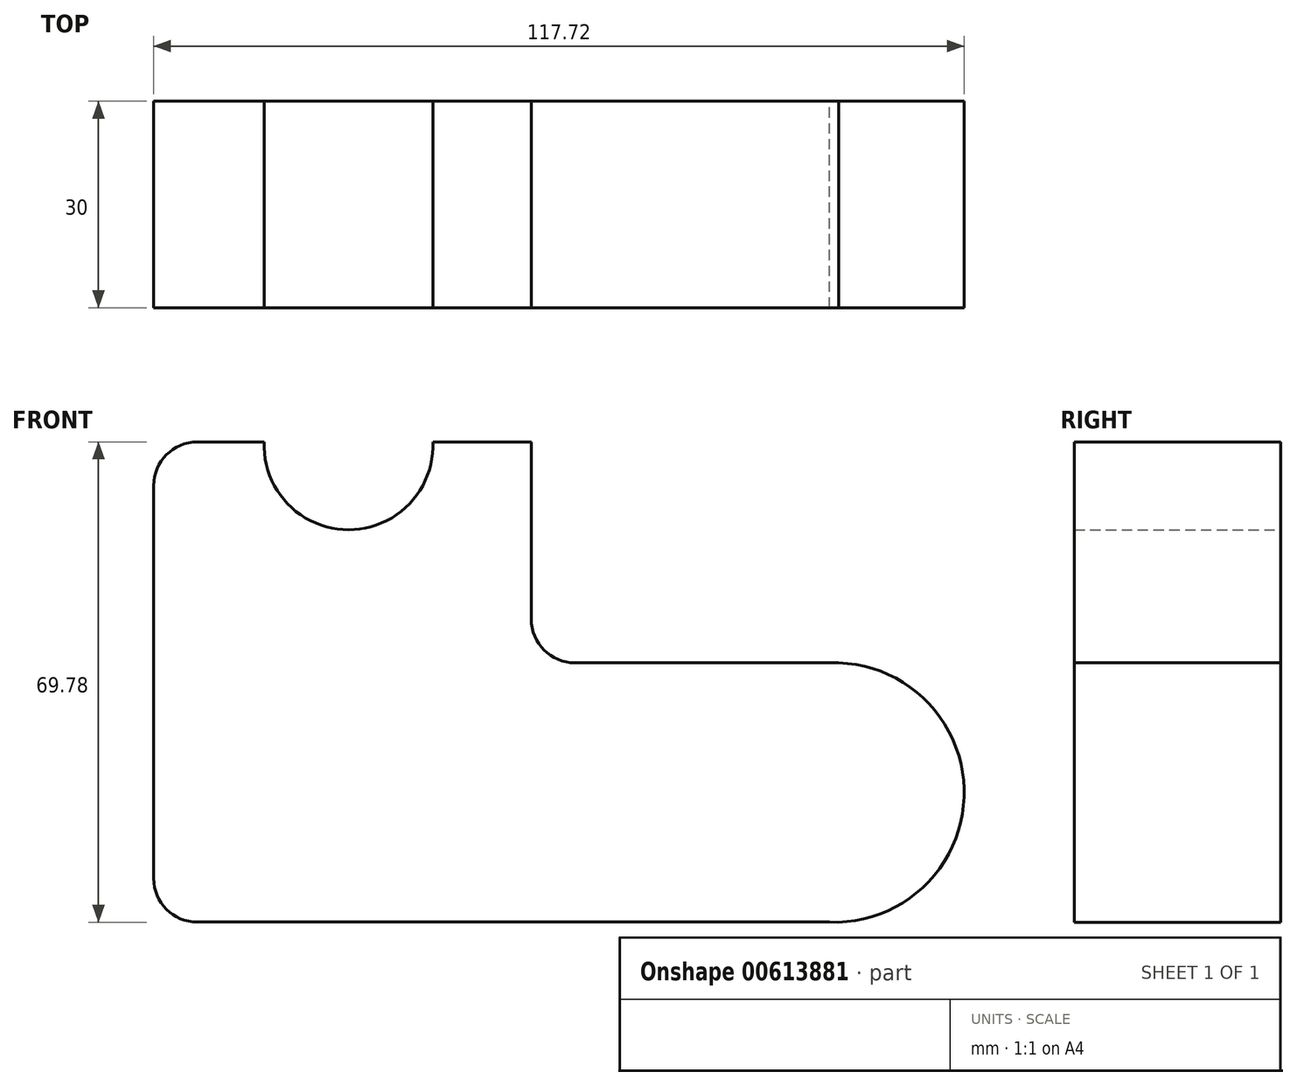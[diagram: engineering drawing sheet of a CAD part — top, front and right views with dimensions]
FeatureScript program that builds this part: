
annotation { "Feature Type Name" : "Feature", "Feature Type Description" : "" }
export const myFeature = defineFeature(function(context is Context, id is Id, definition is map)
    precondition{}
    {
        {
            var Q0;
            Q0=qCreatedBy(makeId("Front.planeOp"),FACE);
            var sketch = newSketch(context, id + "F0", { "sketchPlane" : qUnion([Q0])});
            skLineSegment(sketch, "E0", {"start": v(-14.34, 0) * mm, "end": v(-107.56, 0) * mm});
            skLineSegment(sketch, "E1", {"start": v(-113.9, 6.35) * mm, "end": v(-113.9, 63.42) * mm});
            skLineSegment(sketch, "E2", {"start": v(-107.56, 69.77) * mm, "end": v(-97.86, 69.77) * mm});
            skLineSegment(sketch, "E3", {"start": v(-59.07, 69.77) * mm, "end": v(-59.07, 44.02) * mm});
            skLineSegment(sketch, "E4", {"start": v(-52.72, 37.67) * mm, "end": v(-14.4, 37.67) * mm});
            skLineSegment(sketch, "E5", {"start": v(0, 31.32) * mm, "end": v(0, 30.2) * mm});
            skPoint(sketch, "E6.visualSharp", {"position": v(-113.9, 69.77) * mm});
            skArc(sketch, "E6.filletArc", {"start": v(-107.56, 69.77) * mm, "mid": v(-112.05, 67.91) * mm, "end": v(-113.9, 63.42) * mm});
            skPoint(sketch, "E7.visualSharp", {"position": v(-113.9, 0) * mm});
            skArc(sketch, "E7.filletArc", {"start": v(-113.9, 6.35) * mm, "mid": v(-112.05, 1.86) * mm, "end": v(-107.56, 0) * mm});
            skPoint(sketch, "E8.visualSharp", {"position": v(0, 0) * mm});
            skPoint(sketch, "E9.visualSharp", {"position": v(0, 37.67) * mm});
            skPoint(sketch, "E10.visualSharp", {"position": v(-59.07, 37.67) * mm});
            skArc(sketch, "E10.filletArc", {"start": v(-59.07, 44.02) * mm, "mid": v(-57.21, 39.53) * mm, "end": v(-52.72, 37.67) * mm});
            skArc(sketch, "E11", {"start": v(-15.74, 0) * mm, "mid": v(3.8, 18.16) * mm, "end": v(-14.4, 37.67) * mm});
            skLineSegment(sketch, "E12.trimOffspring", {"start": v(0, 7.47) * mm, "end": v(0, 6.35) * mm});
            skLineSegment(sketch, "E13.trimOffspring", {"start": v(-73.35, 69.77) * mm, "end": v(-59.07, 69.77) * mm});
            skArc(sketch, "E14", {"start": v(-97.86, 69.77) * mm, "mid": v(-85.6, 57) * mm, "end": v(-73.35, 69.77) * mm});
            skSolve(sketch);
        }
        {
            var Q0;
            Q0 = qSketchRegion(id + "F0", true);
            extrude(context, id + "F1", {"entities" : qUnion([Q0]), "depth" : 30 * mm, "offsetDistance" : 25.4 * mm});
        }
    });
